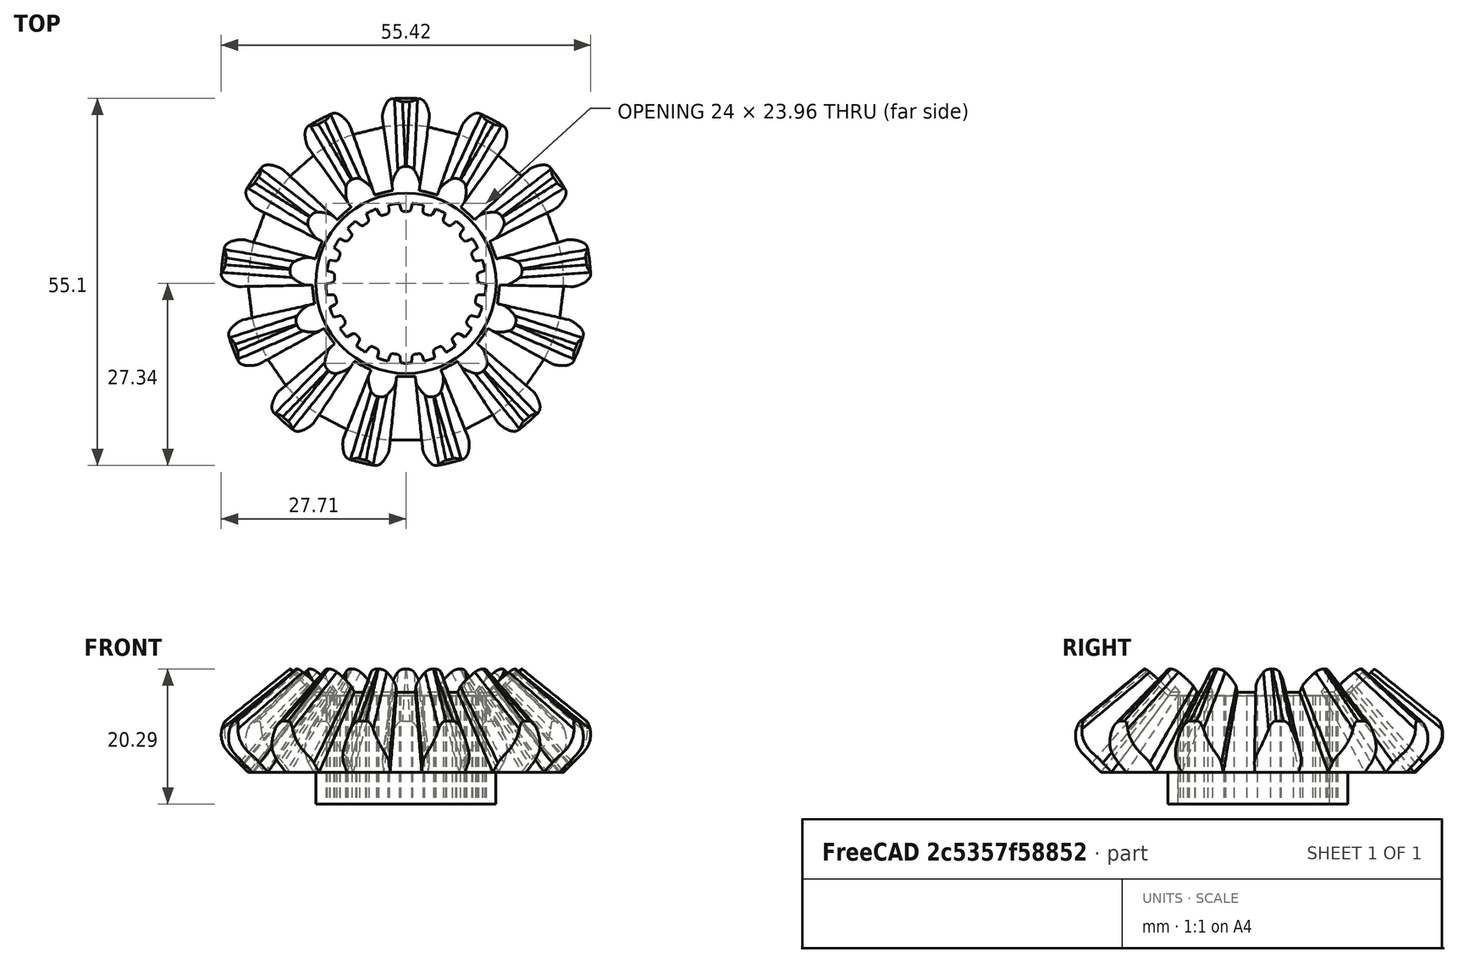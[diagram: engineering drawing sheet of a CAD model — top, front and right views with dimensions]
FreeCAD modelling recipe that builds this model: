
FCSTD DOCUMENT  (FreeCAD 1.0R39319 (Git))
Label: DG Krushna Straight miter gear
License: All rights reserved
LicenseURL: https://en.wikipedia.org/wiki/All_rights_reserved
objects: Sketcher::SketchObject×13, PartDesign::Groove×4, TechDraw::DrawProjGroupItem×3, TechDraw::DrawViewDimension×3, PartDesign::Pad×2, PartDesign::Fillet×2, Part::FeaturePython×1, PartDesign::FeatureBase×1, PartDesign::Pocket×1, PartDesign::PolarPattern×1, PartDesign::Body×1, TechDraw::DrawSVGTemplate×1, TechDraw::DrawProjGroup×1, TechDraw::DrawPage×1
note: 62 computed .brp shape members not serialized (recipe doc carries the construction recipe); baked Part::Feature solids carry a one-line shape summary decoded from their .brp

FEATURE [Part::FeaturePython] BevelGear  # WARN: FeaturePython — macro-defined, semantics opaque (R4)
  AttacherType = Attacher::AttachEngine3D
  angular_backlash = 0
  backlash = 0
  beta = 0
  clearance = 0.1
  dw = 59.15
  height = 15.5
  module = 4.55
  num_teeth = 13
  numpoints = 20
  pitch_angle = 45
  pressure_angle = 20
  reset_origin = true
  version = 1.3.0
  expr: angular_backlash = backlash / dw * 360 ° / pi
  expr: dw = num_teeth * module
FEATURE [PartDesign::FeatureBase] BaseFeature
  BaseFeature = -> BevelGear
  Suppressed = false
FEATURE [Sketcher::SketchObject] Sketch
  ArcFitTolerance = 1e-06
  AttachmentSupport = -> [BaseFeature]
  ExternalGeometry = -> [BaseFeature]
  FullyConstrained = true
  MakeInternals = false
  MapMode = 5
  Placement = pos=(0,0,0) rot=(1,0,0;3.14159rad)
  sketch-geometry (2):
    g0: Circle CenterX=0 CenterY=0 CenterZ=0 NormalX=0 NormalY=0 NormalZ=1 AngleXU=0 Radius=23.6602
    g1: Circle CenterX=0 CenterY=0 CenterZ=0 NormalX=0 NormalY=0 NormalZ=1 AngleXU=0 Radius=36.8272
  constraints (4):
    c: Coincident(g0,g-1)
    c: PointOnObject(g-4,g0)
    c: Coincident(g1,g0)
    c: PointOnObject(g-3,g1)
FEATURE [Sketcher::SketchObject] Sketch001
  ArcFitTolerance = 1e-06
  AttachmentSupport = -> [YZ_Plane]
  ExternalGeometry = -> [Sketch]
  FullyConstrained = true
  MakeInternals = false
  MapMode = 5
  Placement = pos=(0,0,0) rot=(0.57735,0.57735,0.57735;2.0944rad)
  sketch-geometry (3):
    g0: LineSegment StartX=23.6602 StartY=0 StartZ=0 EndX=36.8272 EndY=13.167 EndZ=0
    g1: LineSegment StartX=36.8272 StartY=0 StartZ=0 EndX=36.8272 EndY=13.167 EndZ=0
    g2: LineSegment StartX=23.6602 StartY=0 StartZ=0 EndX=36.8272 EndY=0 EndZ=0
  constraints (7):
    c: Coincident(g0,g-3)
    c: Coincident(g1,g-4)
    c: Vertical(g1)
    c: Coincident(g0,g1)
    c: Angle(g-4,g0) = 0.785398
    c: Coincident(g2,g0)
    c: Coincident(g2,g1)
FEATURE [PartDesign::Groove] Groove
  Angle = 360
  Angle2 = 60
  Axis = (0,0,1)
  Base = (0,0,0)
  BaseFeature = -> BaseFeature
  Profile = -> Sketch001
  ReferenceAxis = -> Sketch001 [V_Axis]
  Refine = true
  Suppressed = false
  Type = 0
FEATURE [Sketcher::SketchObject] Sketch002
  ArcFitTolerance = 1e-06
  AttachmentSupport = -> [Groove]
  ExternalGeometry = -> [Groove]
  FullyConstrained = true
  MakeInternals = false
  MapMode = 5
  Placement = pos=(-3e-16,0,15.5) rot=(0,0,1;0rad)
  sketch-geometry (2):
    g0: Circle CenterX=0 CenterY=0 CenterZ=0 NormalX=0 NormalY=0 NormalZ=1 AngleXU=0 Radius=11.2601
    g1: Circle CenterX=0 CenterY=0 CenterZ=0 NormalX=0 NormalY=0 NormalZ=1 AngleXU=0 Radius=17.5264
  constraints (4):
    c: Coincident(g0,g-1)
    c: PointOnObject(g-3,g0)
    c: Coincident(g1,g0)
    c: PointOnObject(g-4,g1)
FEATURE [Sketcher::SketchObject] Sketch003
  ArcFitTolerance = 1e-06
  AttachmentSupport = -> [YZ_Plane]
  ExternalGeometry = -> [Sketch002]
  FullyConstrained = true
  MakeInternals = false
  MapMode = 5
  Placement = pos=(0,0,0) rot=(0.57735,0.57735,0.57735;2.0944rad)
  sketch-geometry (4):
    g0: LineSegment StartX=17.5264 StartY=15.5 StartZ=0 EndX=13.5264 EndY=11.5 EndZ=0
    g1: LineSegment StartX=13.5264 StartY=11.5 StartZ=0 EndX=0 EndY=11.5 EndZ=0
    g2: LineSegment StartX=0 StartY=11.5 StartZ=0 EndX=2e-16 EndY=15.5 EndZ=0
    g3: LineSegment StartX=-6e-16 StartY=15.5 StartZ=0 EndX=17.5264 EndY=15.5 EndZ=0
  constraints (10):
    c: Coincident(g0,g-4)
    c: Coincident(g1,g0)
    c: PointOnObject(g1,g-2)
    c: Horizontal(g1)
    c: Coincident(g2,g1)
    c: Symmetric(g-4,g-4,g2)
    c: Symmetric(g-4,g-4,g3)
    c: Coincident(g3,g0)
    c: Angle(g3,g0) = 0.785398
    c: Distance(g3,g1) = 4
FEATURE [Sketcher::SketchObject] Sketch005
  ArcFitTolerance = 1e-06
  AttachmentSupport = -> [Groove]
  ExternalGeometry = -> [Groove]
  FullyConstrained = true
  MakeInternals = false
  MapMode = 5
  Placement = pos=(-3e-16,0,15.5) rot=(0,0,1;0rad)
  constraints (1):
    c: Distance(g-3,g-3) = 2.25347
FEATURE [Sketcher::SketchObject] Sketch009
  ArcFitTolerance = 1e-06
  AttachmentSupport = -> [YZ_Plane]
  FullyConstrained = true
  MakeInternals = false
  MapMode = 5
  Placement = pos=(0,0,0) rot=(0.57735,0.57735,0.57735;2.0944rad)
  sketch-geometry (5):
    g0: ArcOfCircle CenterX=29.7006 CenterY=6.73825 CenterZ=0 NormalX=0 NormalY=0 NormalZ=1 AngleXU=0 Radius=4 StartAngle=5.49779 EndAngle=7.17681
    g1: LineSegment StartX=37.529 StartY=3.90983 StartZ=0 EndX=32.529 EndY=3.90983 EndZ=0
    g2: LineSegment StartX=32.207 StartY=9.85564 StartZ=0 EndX=37.529 EndY=9.85564 EndZ=0
    g3: LineSegment StartX=37.529 StartY=9.85564 StartZ=0 EndX=37.529 EndY=3.90983 EndZ=0
    g4: LineSegment [constr] StartX=17.1129 StartY=21.9912 StartZ=0 EndX=35.6814 EndY=7.0622 EndZ=0
  constraints (13):
    c: Tangent(g0,g-3) = -1.5708
    c: Radius(g0) = 4
    c: Coincident(g1,g0)
    c: Coincident(g0,g2)
    c: Coincident(g2,g3)
    c: Coincident(g1,g3)
    c: Horizontal(g2)
    c: Horizontal(g1)
    c: Vertical(g3)
    c: DistanceX(g1,g1) = 5
    c: Coincident(g4,g-4)
    c: Coincident(g4,g-3)
    c: Tangent(g0,g4) = 1.5708
FEATURE [PartDesign::Groove] Groove001
  Angle = 360
  Angle2 = 60
  Axis = (0,0,1)
  Base = (0,0,0)
  BaseFeature = -> Groove
  Profile = -> Sketch003
  ReferenceAxis = -> Sketch003 [V_Axis]
  Refine = true
  Suppressed = false
  Type = 0
FEATURE [Sketcher::SketchObject] Sketch006
  ArcFitTolerance = 1e-06
  AttachmentSupport = -> [Groove001]
  FullyConstrained = true
  MakeInternals = false
  MapMode = 5
  Placement = pos=(0,0,0) rot=(1,0,0;3.14159rad)
  sketch-geometry (1):
    g0: Circle CenterX=0 CenterY=0 CenterZ=0 NormalX=0 NormalY=0 NormalZ=1 AngleXU=0 Radius=13.5
  constraints (2):
    c: Diameter(g0) = 27
    c: Coincident(g0,g-1)
FEATURE [PartDesign::Pad] Pad
  BaseFeature = -> Groove001
  Direction = (0,0,-1)
  Length = 4.8
  Length2 = 10
  Profile = -> Sketch006
  ReferenceAxis = -> Sketch006 [N_Axis]
  Refine = true
  Suppressed = false
  Type = 0
FEATURE [PartDesign::Groove] Groove002
  Angle = 360
  Angle2 = 60
  Axis = (0,0,1)
  Base = (0,0,0)
  BaseFeature = -> Pad
  Profile = -> Sketch009
  ReferenceAxis = -> Sketch009 [V_Axis]
  Refine = true
  Suppressed = false
  Type = 0
FEATURE [Sketcher::SketchObject] Sketch010
  ArcFitTolerance = 1e-06
  AttachmentSupport = -> [Groove002]
  FullyConstrained = true
  MakeInternals = false
  MapMode = 5
  Placement = pos=(0,0,11.5) rot=(0,0,1;0rad)
FEATURE [Sketcher::SketchObject] Sketch011
  ArcFitTolerance = 1e-06
  AttachmentSupport = -> [Groove002]
  FullyConstrained = true
  MakeInternals = false
  MapMode = 5
  Placement = pos=(0,0,11.5) rot=(0,0,1;0rad)
  sketch-geometry (1):
    g0: Circle CenterX=0 CenterY=0 CenterZ=0 NormalX=0 NormalY=0 NormalZ=1 AngleXU=0 Radius=12
  constraints (2):
    c: Diameter(g0) = 24
    c: Coincident(g0,g-1)
FEATURE [PartDesign::Pocket] Pocket
  BaseFeature = -> Groove002
  Direction = (0,0,-1)
  Length = 5
  Length2 = 5
  Profile = -> Sketch011
  ReferenceAxis = -> Sketch011 [N_Axis]
  Refine = true
  Suppressed = false
  Type = 1
FEATURE [Sketcher::SketchObject] Sketch012
  ArcFitTolerance = 1e-06
  AttachmentSupport = -> [Pocket]
  FullyConstrained = true
  MakeInternals = false
  MapMode = 5
  Placement = pos=(0,0,11.5) rot=(0,0,1;0rad)
FEATURE [Sketcher::SketchObject] Sketch013
  ArcFitTolerance = 1e-06
  AttachmentSupport = -> [Pocket]
  ExternalGeometry = -> [Pocket]
  FullyConstrained = true
  MakeInternals = false
  MapMode = 5
  Placement = pos=(0,0,11.5) rot=(0,0,1;0rad)
  sketch-geometry (8):
    g0: ArcOfCircle CenterX=0 CenterY=0 CenterZ=0 NormalX=0 NormalY=0 NormalZ=1 AngleXU=0 Radius=10.75 StartAngle=1.50843 EndAngle=1.63316
    g1: LineSegment [constr] StartX=-2.2602 StartY=13.7367 StartZ=0 EndX=-2.2602 EndY=8.16723 EndZ=0
    g2: LineSegment [constr] StartX=4.20492 StartY=13.7481 StartZ=0 EndX=4.20492 EndY=8.1902 EndZ=0
    g3: LineSegment StartX=-0.67 StartY=10.7291 StartZ=0 EndX=-0.976939 EndY=11.9602 EndZ=0
    g4: LineSegment StartX=0.67 StartY=10.7291 StartZ=0 EndX=0.976939 EndY=11.9602 EndZ=0
    g5: LineSegment [constr] StartX=-0.82347 StartY=11.3446 StartZ=0 EndX=0.82347 EndY=11.3446 EndZ=0
    g6: GeomPoint [constr] X=-8e-16 Y=11.3446 Z=0
    g7: ArcOfCircle CenterX=0 CenterY=0 CenterZ=0 NormalX=0 NormalY=0 NormalZ=1 AngleXU=0 Radius=12 StartAngle=1.48929 EndAngle=1.6523
  constraints (19):
    c: Vertical(g1)
    c: Block(g1)
    c: Block(g2)
    c: DistanceX(g0,g0) = 1.34
    c: Coincident(g3,g0)
    c: Coincident(g4,g0)
    c: Equal(g3,g4)
    c: Angle(g1,g3) = 0.244346
    c: Angle(g4,g2) = 0.244346
    c: Symmetric(g3,g3,g5)
    c: Symmetric(g4,g4,g5)
    c: Horizontal(g5)
    c: Symmetric(g5,g5,g6)
    c: PointOnObject(g3,g-3)
    c: Coincident(g0,g-1)
    c: Coincident(g7,g0)
    c: Coincident(g7,g3)
    c: Coincident(g7,g4)
    c: Radius(g0) = 10.75
FEATURE [PartDesign::Pad] Pad001
  BaseFeature = -> Pocket
  Direction = (0,0,1)
  Length = 10
  Length2 = 10
  Profile = -> Sketch013
  ReferenceAxis = -> Sketch013 [N_Axis]
  Refine = true
  Reversed = true
  Suppressed = false
  Type = 3
  UpToFace = -> Pocket [Face98]
FEATURE [PartDesign::PolarPattern] PolarPattern
  Angle = 360
  Axis = -> Sketch013 [N_Axis]
  BaseFeature = -> Pad001
  Mode = 0
  Occurrences = 21
  Offset = 120
  Originals = -> [Pad001]
  Refine = true
  Suppressed = false
  TransformMode = 0
FEATURE [PartDesign::Fillet] Fillet
  Base = -> PolarPattern [Edge410,Edge463,Edge420,Edge415,Edge423,Edge460,Edge428,Edge457,Edge454,Edge433,Edge438,Edge451,Edge405,Edge466,Edge400,Edge469,Edge395,Edge472,Edge390,Edge475,Edge448,Edge443,Edge506,Edge505,Edge345,Edge502,Edge350,Edge499,Edge355,Edge496,Edge360,Edge493,Edge365,Edge490,Edge487,Edge484,Edge481,Edge478,Edge375,Edge370,+2 more]
  BaseFeature = -> PolarPattern
  Radius = 0.5
  Refine = true
  SupportTransform = false
  Suppressed = false
  UseAllEdges = false
FEATURE [Sketcher::SketchObject] Sketch014
  ArcFitTolerance = 1e-06
  AttachmentSupport = -> [YZ_Plane]
  FullyConstrained = true
  MakeInternals = false
  MapMode = 5
  Placement = pos=(0,0,0) rot=(0.57735,0.57735,0.57735;2.0944rad)
FEATURE [Sketcher::SketchObject] Sketch015
  ArcFitTolerance = 1e-06
  AttachmentSupport = -> [YZ_Plane]
  ExternalGeometry = -> [Fillet]
  FullyConstrained = true
  MakeInternals = false
  MapMode = 5
  Placement = pos=(0,0,0) rot=(0.57735,0.57735,0.57735;2.0944rad)
  sketch-geometry (10):
    g0: LineSegment [constr] StartX=17.5063 StartY=15.5 StartZ=0 EndX=29.5096 EndY=5.84935 EndZ=0
    g1: ArcOfCircle [constr] CenterX=17.5063 CenterY=15.5 CenterZ=0 NormalX=0 NormalY=0 NormalZ=-1 AngleXU=-2.46442 Radius=0.3 StartAngle=1.5708 EndAngle=4.71239
    g2: LineSegment [constr] StartX=17.6942 StartY=15.7338 StartZ=0 EndX=21.6953 EndY=12.5169 EndZ=0
    g3: LineSegment [constr] StartX=21.6953 StartY=12.5169 StartZ=0 EndX=29.6976 EndY=6.08315 EndZ=0
    g4: ArcOfCircle [constr] CenterX=29.5096 CenterY=5.84935 CenterZ=0 NormalX=0 NormalY=0 NormalZ=-1 AngleXU=0.677174 Radius=0.3 StartAngle=1.5708 EndAngle=4.71239
    g5: LineSegment [constr] StartX=21.3194 StartY=12.0493 StartZ=0 EndX=29.3216 EndY=5.61555 EndZ=0
    g6: LineSegment [constr] StartX=17.3183 StartY=15.2662 StartZ=0 EndX=21.3194 EndY=12.0493 EndZ=0
    g7: ArcOfCircle CenterX=23.7421 CenterY=5.73878 CenterZ=0 NormalX=0 NormalY=0 NormalZ=1 AngleXU=0 Radius=4 StartAngle=5.49779 EndAngle=7.17681
    g8: LineSegment StartX=26.5706 StartY=2.91035 StartZ=0 EndX=29.723 EndY=6.06273 EndZ=0
    g9: LineSegment StartX=26.2485 StartY=8.85617 StartZ=0 EndX=29.723 EndY=6.06273 EndZ=0
  constraints (18):
    c: Coincident(g0,g-3)
    c: Coincident(g0,g-4)
    c: Tangent(g1,g2) = 1.5708
    c: Tangent(g1,g6) = -1.5708
    c: Coincident(g2,g3)
    c: Tangent(g3,g4) = 1.5708
    c: Tangent(g4,g5) = -1.5708
    c: Coincident(g5,g6)
    c: Block(g2)
    c: Block(g6)
    c: Block(g5)
    c: Block(g3)
    c: Tangent(g7,g3) = 1.5708
    c: Tangent(g7,g-4) = -1.5708
    c: Radius(g7) = 4
    c: Tangent(g8,g7) = -1.5708
    c: Tangent(g9,g7) = 1.5708
    c: Coincident(g8,g9)
FEATURE [PartDesign::Groove] Groove003
  Angle = 360
  Angle2 = 60
  Axis = (0,0,1)
  Base = (0,0,0)
  BaseFeature = -> Fillet
  Profile = -> Sketch015
  ReferenceAxis = -> Sketch015 [V_Axis]
  Refine = true
  Suppressed = false
  Type = 0
FEATURE [PartDesign::Fillet] Fillet001
  Base = -> Groove003 [Edge518,Edge520,Edge506,Edge504,Edge492,Edge490,Edge532,Edge534,Edge546,Edge548,Edge560,Edge562,Edge574,Edge576,Edge478,Edge476,Edge464,Edge461,Edge632,Edge630,Edge618,Edge616,Edge602,Edge604,Edge590,Edge588]
  BaseFeature = -> Groove003
  Radius = 1.3
  Refine = true
  SupportTransform = false
  Suppressed = false
  UseAllEdges = false
FEATURE [PartDesign::Body] Body
  AllowCompound = false
  BaseFeature = -> BevelGear
  Group = -> [BaseFeature,Sketch,Sketch001,Groove,Sketch002,Sketch003,Sketch005,Groove001,Sketch006,Pad,Sketch009,Groove002,Sketch010,Sketch011,Pocket,Sketch012,Sketch013,Pad001,PolarPattern,Fillet,Sketch014,Sketch015,Groove003,Fillet001]
  Origin = -> Origin
  Tip = -> Fillet001
FEATURE [TechDraw::DrawSVGTemplate] Template
  EditableTexts = AuthorName=Krushna manwatkar; CheckDate=CHECK DATE; CreationDate=06-01-2026; DrawingNumber=NUMBER; FC-Title=DG Krushna Straight miter gear; SheetNumber=1 / 1; Subtitle=SUBTITLE; SupervisorName=SUPERVISOR NAME; Weight=WEIGHT; scale=1 : 1
  Height = 297
  Orientation = 1
  Template = C:/Program Files/FreeCAD 1.0/data/Mod/TechDraw/Templates/A3_Landscape_TD.svg
  Width = 420
FEATURE [TechDraw::DrawProjGroupItem] View  label="Front"
  CoarseView = false
  Direction = (0,-1,0)
  Focus = 100
  HardHidden = false
  IsoCount = 0
  IsoHidden = false
  IsoVisible = false
  LockPosition = true
  Perspective = false
  Rotation = 0
  RotationVector = (1,0,0)
  Scale = 2
  ScaleType = 2
  ScrubCount = 1
  SeamHidden = false
  SeamVisible = false
  SmoothHidden = false
  SmoothVisible = true
  Source = -> [Body]
  Type = 0
  X = 0
  XDirection = (1,0,0)
  Y = 0
FEATURE [TechDraw::DrawProjGroupItem] ProjItem  label="Bottom"
  CoarseView = false
  Direction = (0,0,-1)
  Focus = 100
  HardHidden = false
  IsoCount = 0
  IsoHidden = false
  IsoVisible = false
  LockPosition = false
  Perspective = false
  Rotation = 0
  RotationVector = (1,0,0)
  Scale = 2
  ScaleType = 2
  ScrubCount = 1
  SeamHidden = false
  SeamVisible = false
  SmoothHidden = false
  SmoothVisible = true
  Source = -> [Body]
  Type = 5
  X = 0
  XDirection = (1,0,0)
  Y = -90.3923
FEATURE [TechDraw::DrawProjGroupItem] ProjItem002  label="FrontBottomRight"
  CoarseView = false
  Direction = (0.57735,-0.57735,-0.57735)
  Focus = 100
  HardHidden = false
  IsoCount = 0
  IsoHidden = false
  IsoVisible = false
  LockPosition = false
  Perspective = false
  Rotation = 0
  RotationVector = (1,0,0)
  Scale = 2
  ScaleType = 2
  ScrubCount = 1
  SeamHidden = false
  SeamVisible = false
  SmoothHidden = false
  SmoothVisible = true
  Source = -> [Body]
  Type = 9
  X = 125.75
  XDirection = (0.707107,0.707107,0)
  Y = -90.3923
FEATURE [TechDraw::DrawProjGroup] ProjGroup
  Anchor = -> View
  AutoDistribute = true
  LockPosition = false
  ProjectionType = 1
  Rotation = 0
  Scale = 2
  ScaleType = 1
  Source = -> [Body]
  Views = -> [View,ProjItem,ProjItem002]
  X = 118.988
  Y = 239.141
  spacingX = 15
  spacingY = 15
FEATURE [TechDraw::DrawViewDimension] Dimension001
  AngleOverride = false
  Arbitrary = false
  ArbitraryTolerances = false
  BoxCorners = (2) [(-55.4227,-55.1012,-1e-07),(55.4227,55.1012,1e-07)]
  EqualTolerance = true
  ExtensionAngle = 0
  FormatSpec = ⌀%.2w
  FormatSpecOverTolerance = %+.2w
  FormatSpecUnderTolerance = %+.2w
  Inverted = false
  LineAngle = 0
  LockPosition = false
  MeasureType = 1
  OverTolerance = 0
  References2D = -> [ProjItem]
  Rotation = 0
  ScaleType = 0
  TheoreticalExact = false
  Type = 5
  UnderTolerance = 0
  X = -47.7577
  Y = -78.9782
FEATURE [TechDraw::DrawViewDimension] Dimension
  AngleOverride = false
  Arbitrary = false
  ArbitraryTolerances = false
  BoxCorners = (2) [(-55.4227,-55.1012,-1e-07),(55.4227,55.1012,1e-07)]
  EqualTolerance = true
  ExtensionAngle = 0
  FormatSpec = %.2w
  FormatSpecOverTolerance = %+.2w
  FormatSpecUnderTolerance = %+.2w
  Inverted = false
  LineAngle = 0
  LockPosition = false
  MeasureType = 1
  OverTolerance = 0
  References2D = -> [ProjItem]
  Rotation = 0
  ScaleType = 0
  TheoreticalExact = false
  Type = 8
  UnderTolerance = 0
  X = 128.52
  Y = 69.9982
FEATURE [TechDraw::DrawViewDimension] Dimension002
  AngleOverride = false
  Arbitrary = false
  ArbitraryTolerances = false
  BoxCorners = (2) [(-55.4255,-20.2911,-1e-07),(55.4227,20.2911,1e-07)]
  EqualTolerance = true
  ExtensionAngle = 0
  FormatSpec = %.2w
  FormatSpecOverTolerance = %+.2w
  FormatSpecUnderTolerance = %+.2w
  Inverted = false
  LineAngle = 0
  LockPosition = false
  MeasureType = 1
  OverTolerance = 0
  References2D = -> [View]
  Rotation = 0
  ScaleType = 0
  TheoreticalExact = false
  Type = 0
  UnderTolerance = 0
  X = 116.219
  Y = -9.16618
FEATURE [TechDraw::DrawPage] Page
  KeepUpdated = true
  NextBalloonIndex = 1
  ProjectionType = 0
  Template = -> Template
  Views = -> [ProjGroup,Dimension001,Dimension,Dimension002]
